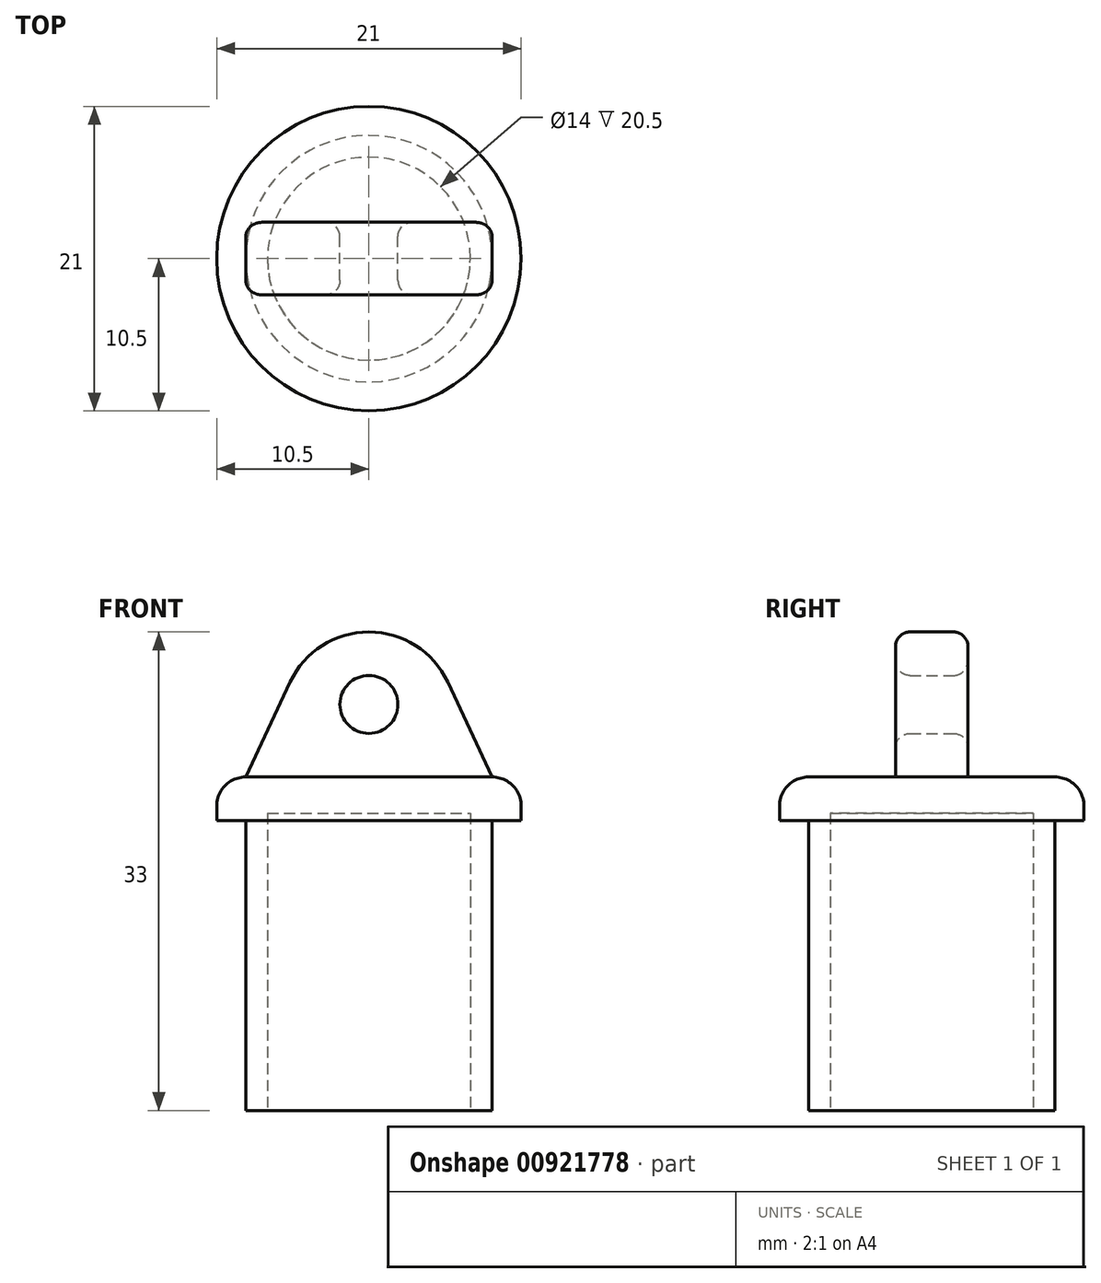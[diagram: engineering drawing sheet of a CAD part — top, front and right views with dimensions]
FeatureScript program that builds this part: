
annotation { "Feature Type Name" : "Feature", "Feature Type Description" : "" }
export const myFeature = defineFeature(function(context is Context, id is Id, definition is map)
    precondition{}
    {
        {
            var Q0;
            Q0=qCreatedBy(makeId("Top.planeOp"),FACE);
            var sketch = newSketch(context, id + "F0", { "sketchPlane" : qUnion([Q0])});
            skCircle(sketch, "E0", {"center": v(0, 0) * mm, "radius": 10.5 * mm});
            skSolve(sketch);
        }
        {
            var Q0;
            Q0 = qSketchRegion(id + "F0", true);
            extrude(context, id + "F1", {"entities" : qUnion([Q0]), "depth" : 3 * mm, "offsetDistance" : 25 * mm});
        }
        {
            var Q0;
            Q0=makeQuery(id+"F1.opExtrude","CAP_EDGE",EDGE,{"disambiguationData":[OSD([sQuery(id+"F0.wireOp",EDGE,"E0")])],"isStart":false});
            fillet(context, id + "F2", {"entities" : qUnion([Q0]), "radius" : 2 * mm, "tangentPropagation" : true, "allowEdgeOverflow" : false});
        }
        {
            var Q0;
            Q0=makeQuery(id+"F1.opExtrude","CAP_FACE",FACE,{"disambiguationData":[OSD([sQuery(id+"F0.wireOp",EDGE,"E0")])],"isStart":true});
            var sketch = newSketch(context, id + "F3", { "sketchPlane" : qUnion([Q0])});
            skCircle(sketch, "E1", {"center": v(0, 0) * mm, "radius": 7 * mm});
            skSolve(sketch);
        }
        {
            var Q0;
            Q0 = qSketchRegion(id + "F3", true);
            extrude(context, id + "F4", {"entities" : qUnion([Q0]), "operationType" : NewBodyOperationType.REMOVE, "oppositeDirection" : true, "depth" : .5 * mm, "offsetDistance" : 25 * mm});
        }
        {
            var Q0;
            Q0=qCreatedBy(makeId("Front.planeOp"),FACE);
            var sketch = newSketch(context, id + "F5", { "sketchPlane" : qUnion([Q0])});
            skLineSegment(sketch, "E2", {"start": v(7, 0) * mm, "end": v(7, -20) * mm});
            skLineSegment(sketch, "E3", {"start": v(7, -20) * mm, "end": v(8.5, -20) * mm});
            skLineSegment(sketch, "E4.direction1", {"start": v(8.5, -20) * mm, "end": v(32.5, -20) * mm, "construction": true});
            skLineSegment(sketch, "E5", {"start": v(0, 0) * mm, "end": v(0, -22.1) * mm, "construction": true});
            skLineSegment(sketch, "E6", {"start": v(8.5, -20) * mm, "end": v(8.5, 0) * mm});
            skLineSegment(sketch, "E7", {"start": v(8.5, 0) * mm, "end": v(7, 0) * mm});
            skSolve(sketch);
        }
        {
            var Q0;
            Q0 = qSketchRegion(id + "F5", true);
            var Q1;
            Q1 = qConstructionFilter(qBodyType(qCreatedBy(id + "F5" ,EDGE), BodyType.WIRE), ConstructionObject.NO);
            var Q2;
            Q2=sQuery(id+"F5.wireOp",EDGE,"E5");
            revolve(context, id + "F6", {"operationType" : NewBodyOperationType.ADD, "surfaceOperationType" : NewSurfaceOperationType.ADD, "entities" : qUnion([Q0]), "surfaceEntities" : qUnion([Q1]), "axis" : qUnion([Q2]), "revolveType" : RevolveType.FULL});
        }
        {
            var Q0;
            Q0=qCreatedBy(makeId("Front.planeOp"),FACE);
            var sketch = newSketch(context, id + "F7", { "sketchPlane" : qUnion([Q0])});
            skLineSegment(sketch, "E8", {"start": v(-8.5, 3) * mm, "end": v(-5.43, 9.55) * mm});
            skLineSegment(sketch, "E9", {"start": v(8.5, 3) * mm, "end": v(5.43, 9.55) * mm});
            skLineSegment(sketch, "E10", {"start": v(-8.5, 3) * mm, "end": v(8.5, 3) * mm});
            skArc(sketch, "E11", {"start": v(5.43, 9.55) * mm, "mid": v(0, 13) * mm, "end": v(-5.43, 9.55) * mm});
            skCircle(sketch, "E12", {"center": v(0, 8) * mm, "radius": 2 * mm});
            skSolve(sketch);
        }
        {
            var Q0;
            Q0 = qSketchRegion(id + "F7", true);
            extrude(context, id + "F8", {"entities" : qUnion([Q0]), "operationType" : NewBodyOperationType.ADD, "depth" : 2.5 * mm, "offsetDistance" : 25 * mm, "hasSecondDirection" : true, "secondDirectionOppositeDirection" : true, "secondDirectionDepth" : 2.5 * mm});
        }
        {
            var Q0;
            Q0=makeQuery(id+"F8.opExtrude","CAP_EDGE",EDGE,{"disambiguationData":[OSD([sQuery(id+"F7.wireOp",EDGE,"E12")])],"isStart":true});
            var Q1;
            Q1=makeQuery(id+"F8.opExtrude","CAP_EDGE",EDGE,{"disambiguationData":[OSD([sQuery(id+"F7.wireOp",EDGE,"E12")])],"isStart":false});
            var Q2;
            Q2=makeQuery(id+"F8.opExtrude","CAP_EDGE",EDGE,{"disambiguationData":[OSD([sQuery(id+"F7.wireOp",EDGE,"E9")])],"isStart":false});
            var Q3;
            Q3=makeQuery(id+"F8.opExtrude","CAP_EDGE",EDGE,{"disambiguationData":[OSD([sQuery(id+"F7.wireOp",EDGE,"E9")])],"isStart":true});
            fillet(context, id + "F9", {"entities" : qUnion([Q0, Q1, Q2, Q3]), "radius" : 1 * mm, "tangentPropagation" : true, "allowEdgeOverflow" : false});
        }
    });
